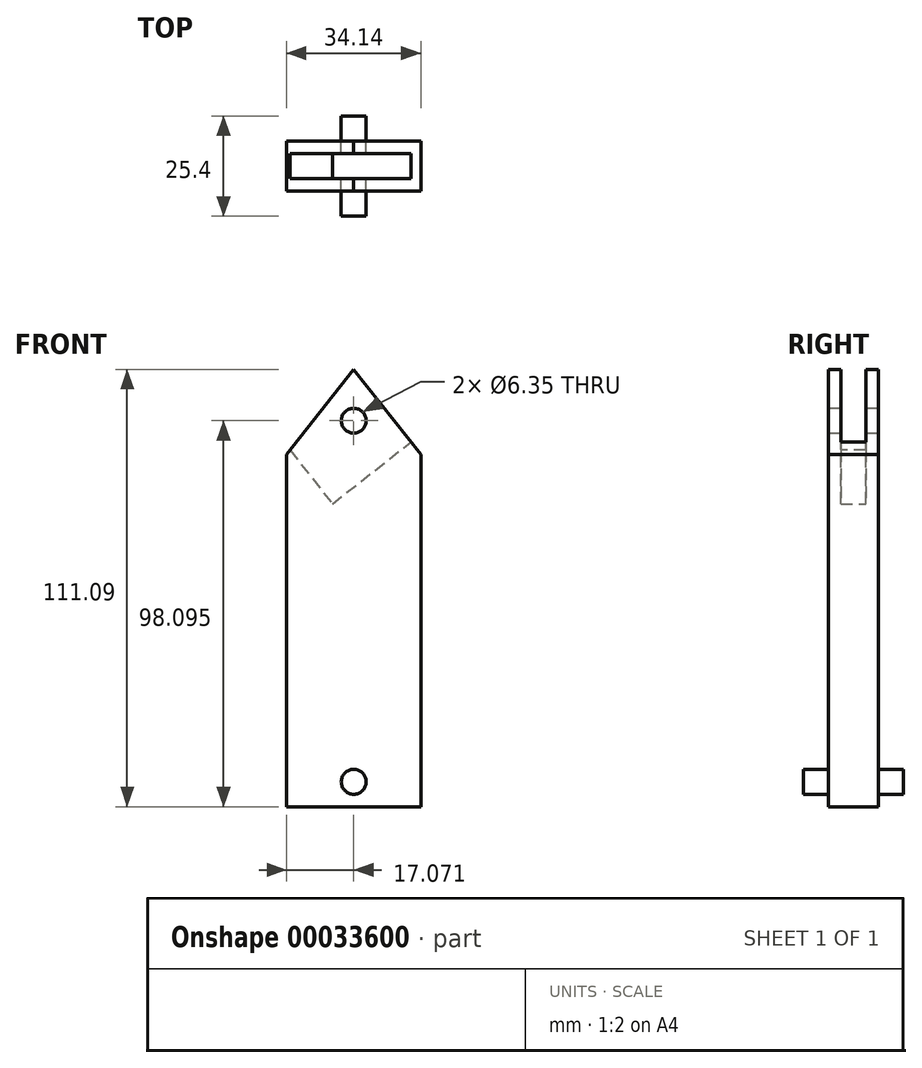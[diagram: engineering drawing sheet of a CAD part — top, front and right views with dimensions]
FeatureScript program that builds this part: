
annotation { "Feature Type Name" : "Feature", "Feature Type Description" : "" }
export const myFeature = defineFeature(function(context is Context, id is Id, definition is map)
    precondition{}
    {
        {
            var Q0;
            Q0=qCreatedBy(makeId("Front.planeOp"),FACE);
            var sketch = newSketch(context, id + "F0", { "sketchPlane" : qUnion([Q0])});
            skLineSegment(sketch, "E0.bottom", {"start": v(-45.2, 64.14) * mm, "end": v(-11.06, 64.14) * mm});
            skLineSegment(sketch, "E0.top", {"start": v(-45.2, -46.95) * mm, "end": v(-11.06, -46.95) * mm});
            skLineSegment(sketch, "E0.left", {"start": v(-45.2, 64.14) * mm, "end": v(-45.2, -46.95) * mm});
            skLineSegment(sketch, "E0.right", {"start": v(-11.06, 64.14) * mm, "end": v(-11.06, -46.95) * mm});
            skLineSegment(sketch, "E1", {"start": v(-28.13, 64.14) * mm, "end": v(-45.2, 42.54) * mm});
            skLineSegment(sketch, "E2", {"start": v(-28.13, 64.14) * mm, "end": v(-11.06, 42.54) * mm});
            skCircle(sketch, "E3", {"center": v(-28.13, 51.14) * mm, "radius": 3.18 * mm});
            skSolve(sketch);
        }
        {
            var Q0;
            {var subQ3=sQuery(id+"F0.wireOp",EDGE,"E0.top");Q0=makeQuery(id+"F0.imprint","IMPRINT",FACE,{"disambiguationData":[TD([[makeQuery(id+"F0.imprint","IMPRINT",EDGE,{"derivedFrom":subQ3}),1.0]])]});}
            extrude(context, id + "F1", {"entities" : qUnion([Q0]), "depth" : 12.7 * mm});
        }
        {
            var Q0;
            Q0=makeQuery(id+"F1.opExtrude","SWEPT_FACE",FACE,{"disambiguationData":[OSD([sQuery(id+"F0.wireOp",EDGE,"E2")])]});
            var sketch = newSketch(context, id + "F2", { "sketchPlane" : qUnion([Q0])});
            skLineSegment(sketch, "E4.bottom", {"start": v(-9.53, 67.77) * mm, "end": v(-3.18, 67.77) * mm});
            skLineSegment(sketch, "E4.top", {"start": v(-9.53, 44.33) * mm, "end": v(-3.18, 44.33) * mm});
            skLineSegment(sketch, "E4.left", {"start": v(-9.53, 67.77) * mm, "end": v(-9.53, 44.33) * mm});
            skLineSegment(sketch, "E4.right", {"start": v(-3.18, 67.77) * mm, "end": v(-3.18, 44.33) * mm});
            skPoint(sketch, "E5", {"position": v(-12.7, 67.77) * mm});
            skPoint(sketch, "E6", {"position": v(0, 67.77) * mm});
            skLineSegment(sketch, "E7", {"start": v(-12.7, 67.77) * mm, "end": v(-9.53, 67.77) * mm});
            skLineSegment(sketch, "E8", {"start": v(-3.18, 67.77) * mm, "end": v(0, 67.77) * mm});
            skSolve(sketch);
        }
        {
            var Q0;
            Q0=makeQuery(id+"F2.imprint","IMPRINT",FACE,{"disambiguationData":[TD([[makeQuery(id+"F2.imprint","IMPRINT",EDGE,{"derivedFrom":sQuery(id+"F2.wireOp",EDGE,"E4.bottom")}),-1.0]])]});
            var Q1;
            Q1=sQuery(id+"F2.wireOp",EDGE,"E4.bottom");
            var Q2;
            Q2=sQuery(id+"F2.wireOp",EDGE,"E4.top");
            var Q3;
            Q3=sQuery(id+"F2.wireOp",EDGE,"E4.left");
            var Q4;
            Q4=sQuery(id+"F2.wireOp",EDGE,"E4.right");
            extrude(context, id + "F3", {"entities" : qUnion([Q0]), "operationType" : NewBodyOperationType.REMOVE, "surfaceEntities" : qUnion([Q1, Q2, Q3, Q4]), "oppositeDirection" : true, "depth" : 25.4 * mm});
        }
        {
            var Q0;
            Q0=makeQuery(id+"F1.opExtrude","CAP_FACE",FACE,{"disambiguationData":[OSD([sQuery(id+"F0.wireOp",EDGE,"E0.top"),sQuery(id+"F0.wireOp",EDGE,"E0.left"),sQuery(id+"F0.wireOp",EDGE,"E0.right"),sQuery(id+"F0.wireOp",EDGE,"E1"),sQuery(id+"F0.wireOp",EDGE,"E2"),sQuery(id+"F0.wireOp",EDGE,"E3")])],"isStart":true});
            var sketch = newSketch(context, id + "F4", { "sketchPlane" : qUnion([Q0])});
            skCircle(sketch, "E9", {"center": v(28.13, -40.6) * mm, "radius": 3.18 * mm});
            skPoint(sketch, "E9.centerSnap0", {"position": v(28.13, -46.95) * mm});
            skSolve(sketch);
        }
        {
            var Q0;
            Q0=makeQuery(id+"F1.opExtrude","CAP_FACE",FACE,{"disambiguationData":[OSD([sQuery(id+"F0.wireOp",EDGE,"E0.top"),sQuery(id+"F0.wireOp",EDGE,"E0.left"),sQuery(id+"F0.wireOp",EDGE,"E0.right"),sQuery(id+"F0.wireOp",EDGE,"E1"),sQuery(id+"F0.wireOp",EDGE,"E2"),sQuery(id+"F0.wireOp",EDGE,"E3")])],"isStart":false});
            var sketch = newSketch(context, id + "F5", { "sketchPlane" : qUnion([Q0])});
            skCircle(sketch, "E10", {"center": v(-28.13, -40.6) * mm, "radius": 3.18 * mm});
            skPoint(sketch, "E10.centerSnap0", {"position": v(-28.13, -46.95) * mm});
            skSolve(sketch);
        }
        {
            var Q0;
            Q0 = qSketchRegion(id + "F4", true);
            extrude(context, id + "F6", {"entities" : qUnion([Q0]), "operationType" : NewBodyOperationType.ADD, "depth" : 6.35 * mm});
        }
        {
            var Q0;
            Q0 = qSketchRegion(id + "F5", true);
            extrude(context, id + "F7", {"entities" : qUnion([Q0]), "operationType" : NewBodyOperationType.ADD, "depth" : 6.35 * mm});
        }
    });
